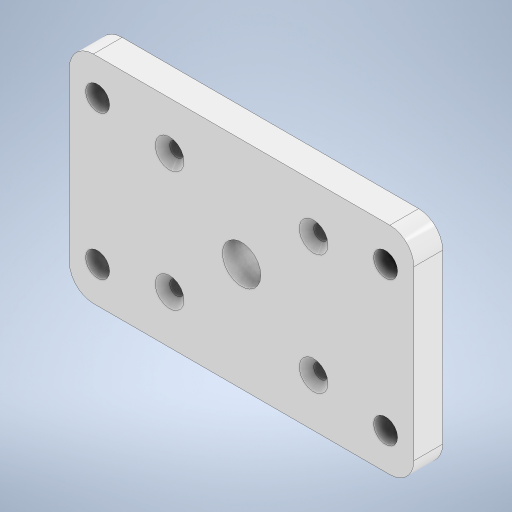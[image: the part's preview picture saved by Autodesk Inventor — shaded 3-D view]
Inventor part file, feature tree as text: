
AUTODESK INVENTOR PART (.ipt)
format: ipt  version: 2023 (Build 270158000, 158)  size: 308,736 bytes
history: native  units: mm
features: extrude x6, sketch x6, chamfer x2, thicken_offset x1
ambient origin geometry x8: Origin, YZ Plane, XZ Plane, XY Plane, X Axis, Y Axis, Z Axis, Center Point
bodies: Solid1 (feature_tree)
feature tree (15):
  extrude  "Extrusion1"  Depth=16.0mm
  extrude  "Extrusion2"  Depth=13.25mm TaperAngle=0.0deg
  extrude  "Extrusion3"  Depth=22.0mm
  extrude  "Extrusion4"  Depth=49.75mm TaperAngle=0.0deg
  thicken_offset  "Thicken1"
  extrude  "Extrusion5"  Depth=15.0mm
  extrude  "Extrusion6"  Depth=1.5mm
  chamfer  "Chamfer2"  Distance=10.0mm
  sketch  "Sketch1"  dims[d0=5.75mm d1=0.0mm d2=16.0mm]
  sketch  "Sketch2"  dims[d3=16.0mm d4=13.25mm d5=0.0mm]
  sketch  "Sketch3"  dims[d6=49.75mm d7=0.0mm d8=22.0mm]
  sketch  "Sketch4"  dims[d9=52.0mm d10=49.75mm d11=0.0mm]
  sketch  "Sketch6"  dims[d12=2.0mm d13=2.0mm d14=15.0mm]
  sketch  "Sketch7"  dims[d15=10.0mm d16=3.0mm d17=10.0mm d18=0.0mm d22=22.5mm d23=8.0mm d24=10.0mm d25=0.0mm d26=25.0mm d27=3.0mm d28=1.5mm d29=2.0mm d30=45.0deg]
  chamfer  "Chamfer3"  Distance=22.5mm
